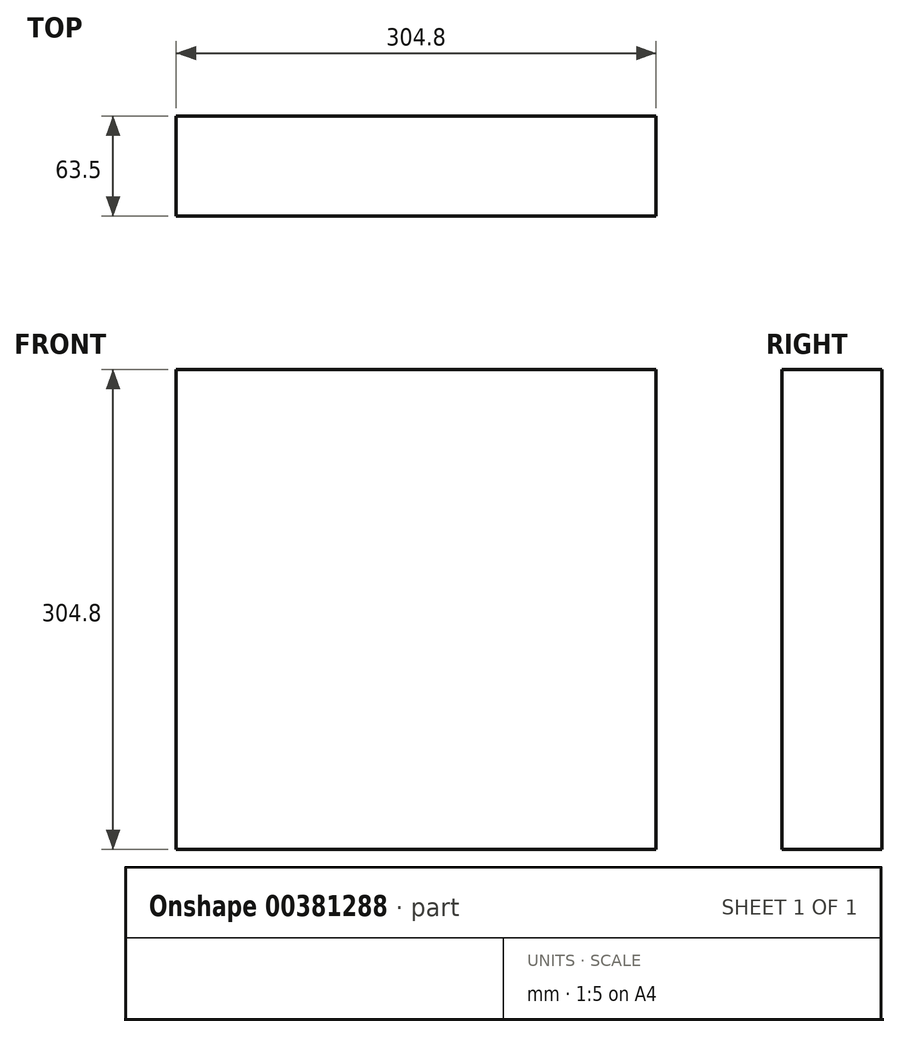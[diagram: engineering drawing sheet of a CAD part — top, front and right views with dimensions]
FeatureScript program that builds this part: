
annotation { "Feature Type Name" : "Feature", "Feature Type Description" : "" }
export const myFeature = defineFeature(function(context is Context, id is Id, definition is map)
    precondition{}
    {
        {
            var Q0;
            Q0=qCreatedBy(makeId("Front.planeOp"),FACE);
            var sketch = newSketch(context, id + "F0", { "sketchPlane" : qUnion([Q0])});
            skLineSegment(sketch, "E0.bottom", {"start": v(-153.3, 179.29) * mm, "end": v(151.5, 179.29) * mm});
            skLineSegment(sketch, "E0.top", {"start": v(-153.3, -125.51) * mm, "end": v(151.5, -125.51) * mm});
            skLineSegment(sketch, "E0.left", {"start": v(-153.3, 179.29) * mm, "end": v(-153.3, -125.51) * mm});
            skLineSegment(sketch, "E0.right", {"start": v(151.5, 179.29) * mm, "end": v(151.5, -125.51) * mm});
            skSolve(sketch);
        }
        {
            var Q0;
            Q0=makeQuery(id+"F0.imprint","IMPRINT",FACE,{"disambiguationData":[TD([[makeQuery(id+"F0.imprint","IMPRINT",EDGE,{"derivedFrom":sQuery(id+"F0.wireOp",EDGE,"E0.bottom")}),-1.0]])]});
            extrude(context, id + "F1", {"entities" : qUnion([Q0]), "depth" : 63.5 * mm});
        }
    });
